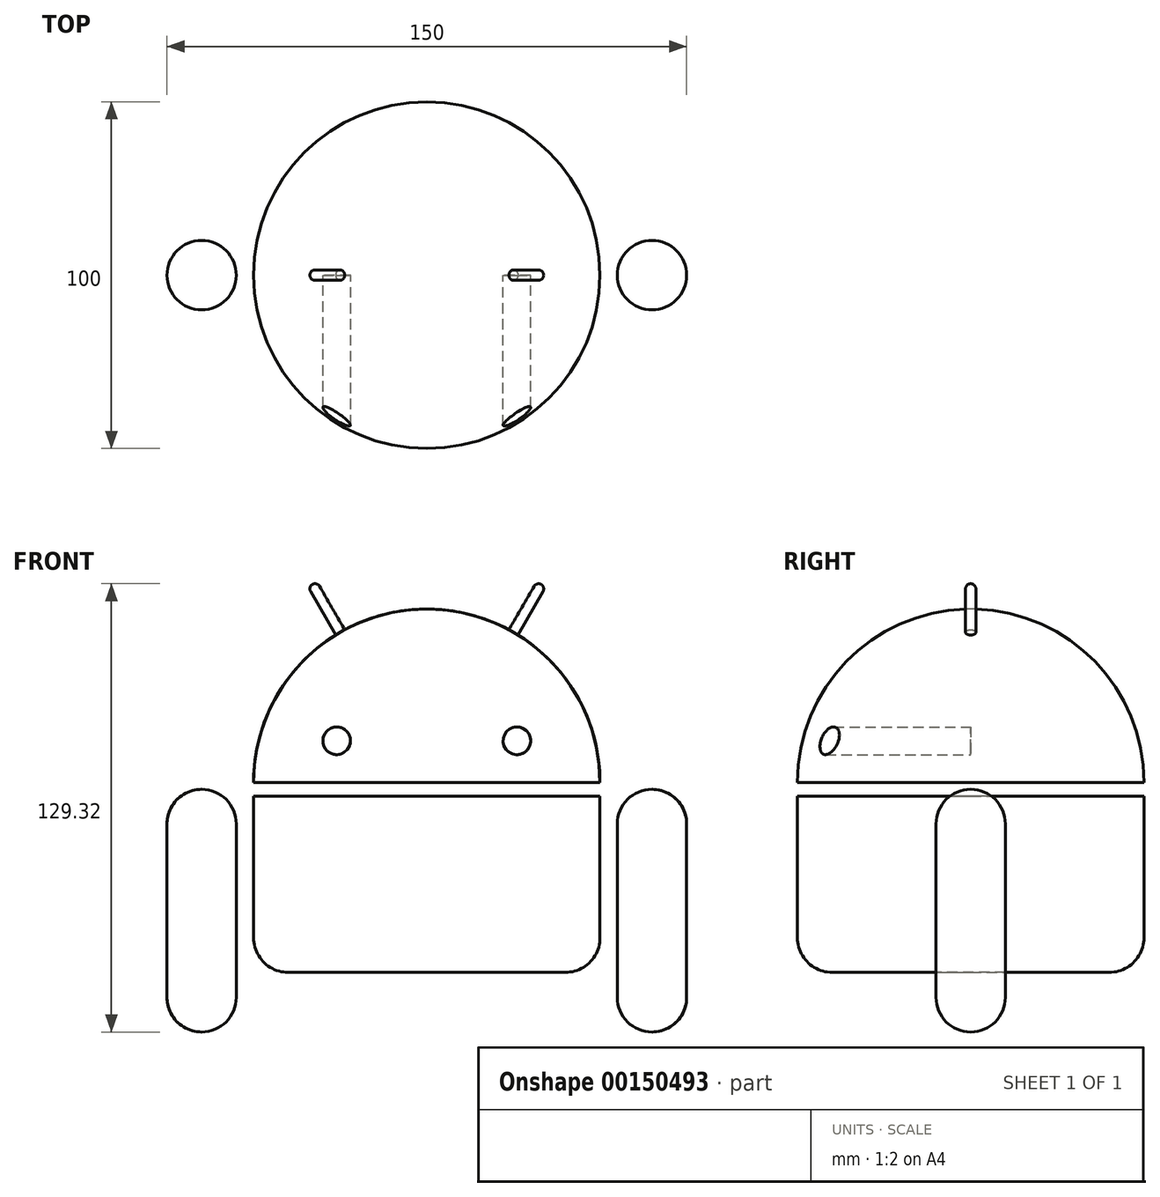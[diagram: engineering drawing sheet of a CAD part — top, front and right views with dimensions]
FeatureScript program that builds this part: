
annotation { "Feature Type Name" : "Feature", "Feature Type Description" : "" }
export const myFeature = defineFeature(function(context is Context, id is Id, definition is map)
    precondition{}
    {
        {
            var Q0;
            Q0=qCreatedBy(makeId("Front.planeOp"),FACE);
            var sketch = newSketch(context, id + "F0", { "sketchPlane" : qUnion([Q0])});
            skLineSegment(sketch, "E0", {"start": v(0, 63.5) * mm, "end": v(0, -112.89) * mm, "construction": true});
            skLineSegment(sketch, "E1", {"start": v(0, 0) * mm, "end": v(50, 0) * mm});
            skLineSegment(sketch, "E2", {"start": v(50, 0) * mm, "end": v(50, -40.8) * mm});
            skLineSegment(sketch, "E3", {"start": v(40, -50.8) * mm, "end": v(0, -50.8) * mm});
            skLineSegment(sketch, "E4", {"start": v(0, -50.8) * mm, "end": v(0, 0) * mm});
            skLineSegment(sketch, "E5", {"start": v(0, 4) * mm, "end": v(50, 4) * mm});
            skLineSegment(sketch, "E6", {"start": v(0, 4) * mm, "end": v(0, 54) * mm});
            skArc(sketch, "E7", {"start": v(50, 4) * mm, "mid": v(35.36, 39.36) * mm, "end": v(0, 54) * mm});
            skLineSegment(sketch, "E8", {"start": v(0, 54) * mm, "end": v(-42.59, 54) * mm, "construction": true});
            skPoint(sketch, "E9.visualSharp", {"position": v(50, -50.8) * mm});
            skArc(sketch, "E9.filletArc", {"start": v(40, -50.8) * mm, "mid": v(47.07, -47.87) * mm, "end": v(50, -40.8) * mm});
            skSolve(sketch);
        }
        {
            var Q0;
            Q0=makeQuery(id+"F0.imprint","IMPRINT",FACE,{"disambiguationData":[TD([[makeQuery(id+"F0.imprint","IMPRINT",EDGE,{"derivedFrom":sQuery(id+"F0.wireOp",EDGE,"E5")}),1.0]])]});
            var Q1;
            Q1=makeQuery(id+"F0.imprint","IMPRINT",FACE,{"disambiguationData":[TD([[makeQuery(id+"F0.imprint","IMPRINT",EDGE,{"derivedFrom":sQuery(id+"F0.wireOp",EDGE,"E1")}),-1.0]])]});
            var Q2;
            Q2=sQuery(id+"F0.wireOp",EDGE,"E0");
            revolve(context, id + "F1", {"entities" : qUnion([Q0, Q1]), "axis" : qUnion([Q2]), "revolveType" : RevolveType.FULL});
        }
        {
            var Q0;
            Q0=qCreatedBy(makeId("Front.planeOp"),FACE);
            var sketch = newSketch(context, id + "F2", { "sketchPlane" : qUnion([Q0])});
            skLineSegment(sketch, "E10", {"start": v(65, 12.15) * mm, "end": v(65, -85.61) * mm, "construction": true});
            skLineSegment(sketch, "E11.bottom", {"start": v(65, -68) * mm, "end": v(65, -68) * mm});
            skLineSegment(sketch, "E11.top", {"start": v(65, 2) * mm, "end": v(65, 2) * mm});
            skLineSegment(sketch, "E11.left", {"start": v(65, -68) * mm, "end": v(65, 2) * mm});
            skLineSegment(sketch, "E11.right", {"start": v(75, -58) * mm, "end": v(75, -8) * mm});
            skPoint(sketch, "E12.visualSharp", {"position": v(75, -68) * mm});
            skArc(sketch, "E12.filletArc", {"start": v(65, -68) * mm, "mid": v(72.07, -65.07) * mm, "end": v(75, -58) * mm});
            skPoint(sketch, "E13.visualSharp", {"position": v(75, 2) * mm});
            skArc(sketch, "E13.filletArc", {"start": v(75, -8) * mm, "mid": v(72.07, -0.93) * mm, "end": v(65, 2) * mm});
            skSolve(sketch);
        }
        {
            var Q0;
            Q0=qSketchRegion(id+"F2",true);
            var Q1;
            Q1=sQuery(id+"F2.wireOp",EDGE,"E10");
            revolve(context, id + "F3", {"entities" : qUnion([Q0]), "axis" : qUnion([Q1]), "revolveType" : RevolveType.FULL});
        }
        {
            var Q0;
            Q0=qCreatedBy(makeId("Front.planeOp"),FACE);
            var sketch = newSketch(context, id + "F4", { "sketchPlane" : qUnion([Q0])});
            skLineSegment(sketch, "E14", {"start": v(0, 3.96) * mm, "end": v(16.28, 32.17) * mm, "construction": true});
            skLineSegment(sketch, "E15", {"start": v(23, 43.8) * mm, "end": v(24.3, 43.05) * mm});
            skLineSegment(sketch, "E16", {"start": v(24.3, 43.05) * mm, "end": v(33.55, 59.07) * mm});
            skLineSegment(sketch, "E17", {"start": v(33, 61.12) * mm, "end": v(33, 61.12) * mm});
            skLineSegment(sketch, "E18", {"start": v(33, 61.12) * mm, "end": v(23, 43.8) * mm});
            skPoint(sketch, "E19.visualSharp", {"position": v(34.3, 60.37) * mm});
            skArc(sketch, "E19.filletArc", {"start": v(33.55, 59.07) * mm, "mid": v(33.7, 60.2) * mm, "end": v(33, 61.12) * mm});
            skSolve(sketch);
        }
        {
            var Q0;
            Q0=qSketchRegion(id+"F4",true);
            var Q1;
            Q1=sQuery(id+"F4.wireOp",EDGE,"E14");
            revolve(context, id + "F5", {"operationType" : NewBodyOperationType.ADD, "entities" : qUnion([Q0]), "axis" : qUnion([Q1]), "revolveType" : RevolveType.FULL});
        }
        {
            var Q0;
            Q0=makeQuery(id+"F3.opRevolve","SWEPT_BODY",BODY,{"disambiguationData":[OSD([sQuery(id+"F2.wireOp",EDGE,"E11.left"),sQuery(id+"F2.wireOp",EDGE,"E11.right"),sQuery(id+"F2.wireOp",EDGE,"E12.filletArc"),sQuery(id+"F2.wireOp",EDGE,"E13.filletArc")])]});
            var Q1;
            Q1=makeQuery(id+"F1.opRevolve","SWEPT_BODY",BODY,{"disambiguationData":[OSD([sQuery(id+"F0.wireOp",EDGE,"E1"),sQuery(id+"F0.wireOp",EDGE,"E2"),sQuery(id+"F0.wireOp",EDGE,"E3"),sQuery(id+"F0.wireOp",EDGE,"E4"),sQuery(id+"F0.wireOp",EDGE,"E9.filletArc")])]});
            var Q2;
            Q2=makeQuery(id+"F1.opRevolve","SWEPT_BODY",BODY,{"disambiguationData":[OSD([sQuery(id+"F0.wireOp",EDGE,"E5"),sQuery(id+"F0.wireOp",EDGE,"E6"),sQuery(id+"F0.wireOp",EDGE,"E7")])]});
            var Q3;
            Q3=qCreatedBy(makeId("Right.planeOp"),FACE);
            mirror(context, id + "F6", {"entities" : qUnion([Q0, Q1, Q2]), "mirrorPlane" : qUnion([Q3])});
        }
        {
            var Q0;
            Q0=qCreatedBy(makeId("Front.planeOp"),FACE);
            var sketch = newSketch(context, id + "F7", { "sketchPlane" : qUnion([Q0])});
            skCircle(sketch, "E20", {"center": v(26, 16) * mm, "radius": 4 * mm});
            skCircle(sketch, "E21", {"center": v(-26, 16) * mm, "radius": 4 * mm});
            skSolve(sketch);
        }
        {
            var Q0;
            Q0=qSketchRegion(id+"F7",true);
            extrude(context, id + "F8", {"entities" : qUnion([Q0]), "operationType" : NewBodyOperationType.REMOVE, "depth" : 60 * mm});
        }
    });
